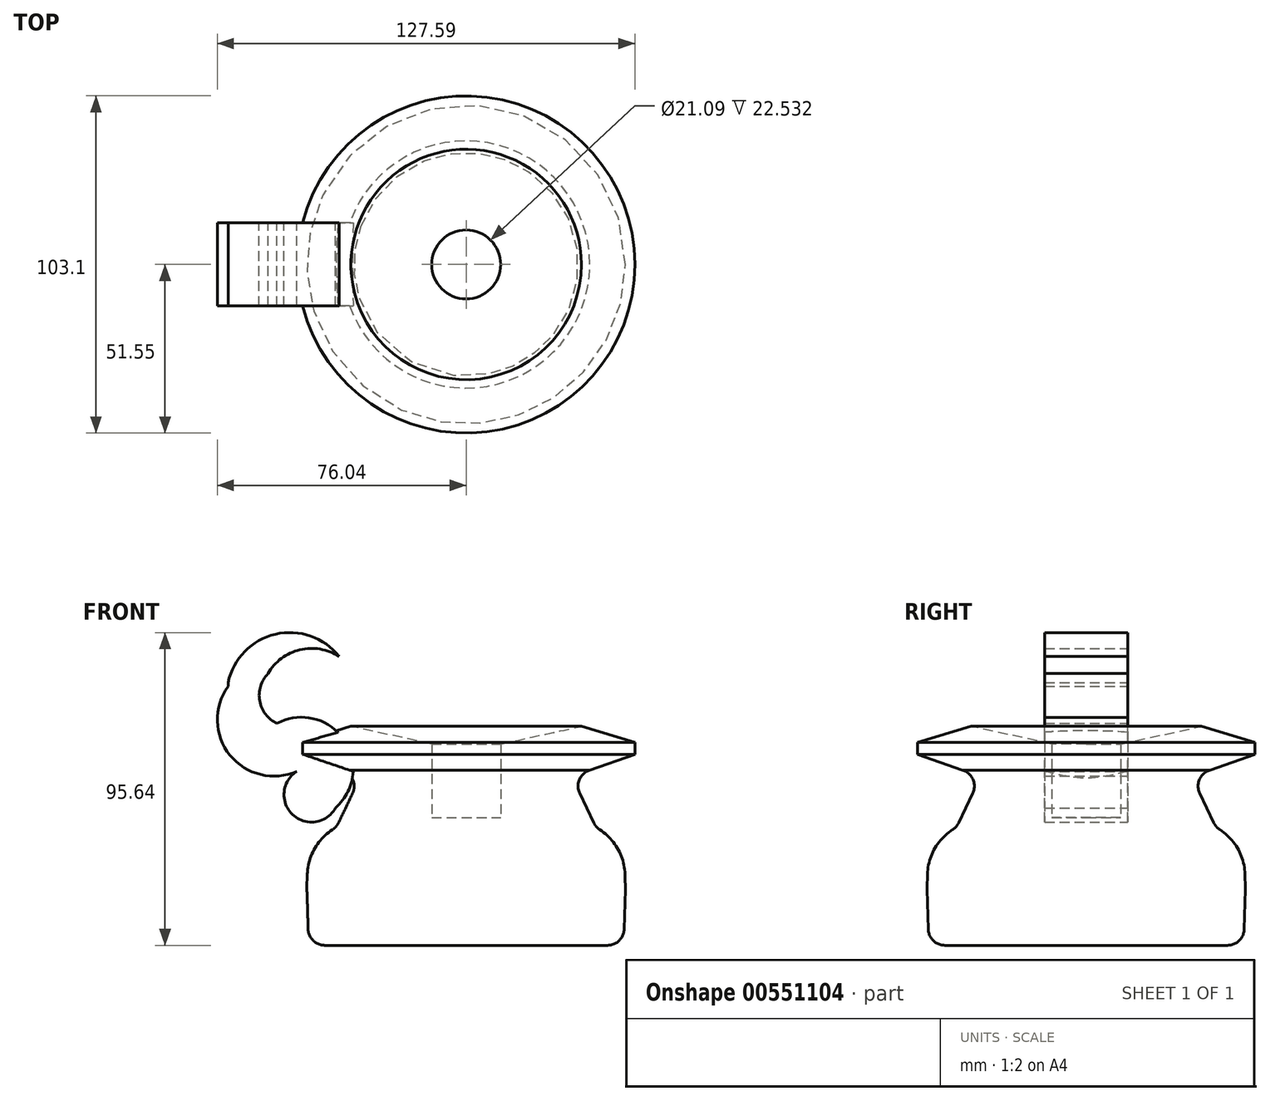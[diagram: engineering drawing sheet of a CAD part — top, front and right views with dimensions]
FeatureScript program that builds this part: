
annotation { "Feature Type Name" : "Feature", "Feature Type Description" : "" }
export const myFeature = defineFeature(function(context is Context, id is Id, definition is map)
    precondition{}
    {
        {
            var Q0;
            Q0=qCreatedBy(makeId("Front.planeOp"),FACE);
            var sketch = newSketch(context, id + "F0", { "sketchPlane" : qUnion([Q0])});
            skLineSegment(sketch, "E0", {"start": v(-51.55, 36.84) * mm, "end": v(-51.55, 20.07) * mm});
            skLineSegment(sketch, "E1", {"start": v(-51.55, 20.07) * mm, "end": v(-31.21, 20.07) * mm});
            skLineSegment(sketch, "E2", {"start": v(-31.21, 20.07) * mm, "end": v(-48.68, -16.43) * mm});
            skLineSegment(sketch, "E3", {"start": v(-48.68, -16.43) * mm, "end": v(0, -16.43) * mm});
            skLineSegment(sketch, "E4", {"start": v(0, -16.43) * mm, "end": v(0, 5.32) * mm});
            skLineSegment(sketch, "E5", {"start": v(-51.55, 36.84) * mm, "end": v(-10.54, 27.86) * mm});
            skLineSegment(sketch, "E6", {"start": v(-10.54, 27.86) * mm, "end": v(-10.54, 5.32) * mm});
            skLineSegment(sketch, "E7", {"start": v(-10.54, 5.32) * mm, "end": v(0, 5.32) * mm});
            skPoint(sketch, "E8.orphan", {"position": v(0, 26.37) * mm});
            skSolve(sketch);
        }
        {
            var Q0;
            Q0 = qSketchRegion(id + "F0", true);
            var Q1;
            Q1=sQuery(id+"F0.wireOp",EDGE,"E4");
            revolve(context, id + "F1", {"entities" : qUnion([Q0]), "axis" : qUnion([Q1]), "revolveType" : RevolveType.FULL});
        }
        {
            var Q0;
            Q0=makeQuery(id+"F1.opRevolve","SWEPT_FACE",FACE,{"disambiguationData":[OSD([sQuery(id+"F0.wireOp",EDGE,"E3")])]});
            var Q1;
            Q1=makeQuery(id+"F1.opRevolve","SWEPT_FACE",FACE,{"disambiguationData":[OSD([sQuery(id+"F0.wireOp",EDGE,"E3")])]});
            extrude(context, id + "F2", {"entities" : qUnion([Q0]), "operationType" : NewBodyOperationType.ADD, "endBound" : BoundingType.SYMMETRIC, "depth" : 34.54 * mm, "endBoundEntityFace" : qUnion([Q1]), "offsetDistance" : 25.4 * mm, "hasDraft" : true, "draftAngle" : 1.8 * degree, "draftPullDirection" : true});
        }
        {
            var Q0;
            Q0=makeQuery(id+"F2.*.split.splitOp","SPLIT",FACE,{"derivedFrom":makeQuery(id+"F2.opExtrude","SWEPT_FACE",FACE,{"disambiguationData":[OSD([sQuery(id+"F0.wireOp",EDGE,"E2"),sQuery(id+"F0.wireOp",EDGE,"E3")])]})});
            fillet(context, id + "F3", {"entities" : qUnion([Q0]), "radius" : 5.08 * mm, "tangentPropagation" : true, "allowEdgeOverflow" : false});
        }
        {
            var Q0;
            Q0=makeQuery(id+"F1.opRevolve","SWEPT_FACE",FACE,{"disambiguationData":[OSD([sQuery(id+"F0.wireOp",EDGE,"E2")])]});
            fillet(context, id + "F4", {"entities" : qUnion([Q0]), "radius" : 5.08 * mm, "tangentPropagation" : true, "allowEdgeOverflow" : false});
        }
        {
            var Q0;
            Q0=makeQuery(id+"F2.*.split.splitOp","SPLIT",FACE,{"derivedFrom":makeQuery(id+"F2.opExtrude","SWEPT_FACE",FACE,{"disambiguationData":[OSD([sQuery(id+"F0.wireOp",EDGE,"E2"),sQuery(id+"F0.wireOp",EDGE,"E3")])]}),"isFromBackBody":true});
            var Q1;
            Q1=makeQuery(id+"F2.*.split.splitOp","SPLIT",FACE,{"derivedFrom":makeQuery(id+"F2.opExtrude","SWEPT_FACE",FACE,{"disambiguationData":[OSD([sQuery(id+"F0.wireOp",EDGE,"E2"),sQuery(id+"F0.wireOp",EDGE,"E3")])]})});
            fillet(context, id + "F5", {"entities" : qUnion([Q0, Q1]), "radius" : 16.82 * mm, "tangentPropagation" : true, "allowEdgeOverflow" : false});
        }
        {
            var Q0;
            Q0=makeQuery(id+"F1.opRevolve","SWEPT_EDGE",EDGE,{"disambiguationData":[OSD([sQuery(id+"F0.wireOp",EDGE,"E0"),sQuery(id+"F0.wireOp",EDGE,"E1")])]});
            var Q1;
            Q1=makeQuery(id+"F1.opRevolve","SWEPT_FACE",FACE,{"disambiguationData":[OSD([sQuery(id+"F0.wireOp",EDGE,"E0")])]});
            chamfer(context, id + "F6", {"entities" : qUnion([Q0, Q1]), "chamferType" : ChamferType.TWO_OFFSETS, "width1" : 5.08 * mm, "oppositeDirection" : true, "width2" : 15.24 * mm, "tangentPropagation" : true});
        }
        {
            var Q0;
            Q0=qCreatedBy(makeId("Front.planeOp"),FACE);
            var sketch = newSketch(context, id + "F7", { "sketchPlane" : qUnion([Q0])});
            skArc(sketch, "E9", {"start": v(-38.82, 54.6) * mm, "mid": v(-50.81, 56.67) * mm, "end": v(-60.57, 49.39) * mm});
            skArc(sketch, "E10", {"start": v(-60.57, 49.39) * mm, "mid": v(-63.1, 41.05) * mm, "end": v(-57.8, 34.13) * mm});
            skArc(sketch, "E11", {"start": v(-39.92, 8.32) * mm, "mid": v(-37.32, 29.22) * mm, "end": v(-57.8, 34.13) * mm});
            skArc(sketch, "E12", {"start": v(-50.3, 20.23) * mm, "mid": v(-53.6, 6.87) * mm, "end": v(-39.92, 8.32) * mm});
            skArc(sketch, "E13", {"start": v(-72.74, 45.48) * mm, "mid": v(-71.68, 23.83) * mm, "end": v(-50.3, 20.23) * mm});
            skArc(sketch, "E14", {"start": v(-38.82, 54.6) * mm, "mid": v(-58.3, 61.42) * mm, "end": v(-72.74, 46.65) * mm});
            skLineSegment(sketch, "E15", {"start": v(-72.74, 46.65) * mm, "end": v(-72.74, 45.48) * mm});
            skSolve(sketch);
        }
        {
            var Q0;
            Q0 = qSketchRegion(id + "F7", true);
            extrude(context, id + "F8", {"entities" : qUnion([Q0]), "operationType" : NewBodyOperationType.ADD, "endBound" : BoundingType.SYMMETRIC, "depth" : 25.4 * mm, "offsetDistance" : 25.4 * mm});
        }
    });
